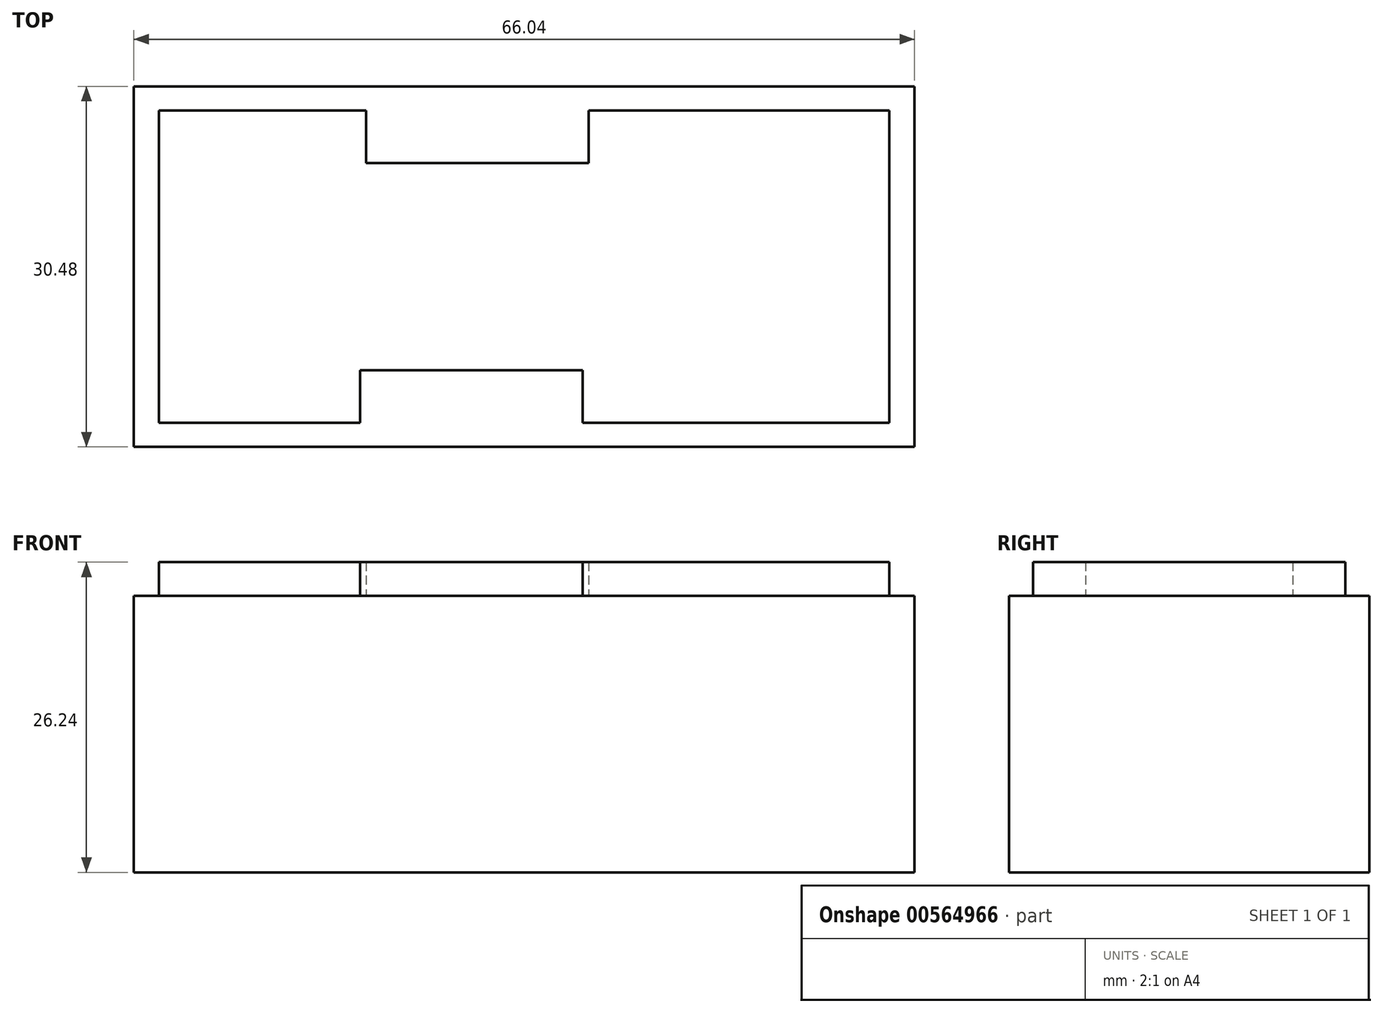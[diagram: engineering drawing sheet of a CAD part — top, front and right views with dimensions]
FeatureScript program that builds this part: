
annotation { "Feature Type Name" : "Feature", "Feature Type Description" : "" }
export const myFeature = defineFeature(function(context is Context, id is Id, definition is map)
    precondition{}
    {
        {
            var Q0;
            Q0=qCreatedBy(makeId("Top.planeOp"),FACE);
            var sketch = newSketch(context, id + "F0", { "sketchPlane" : qUnion([Q0])});
            skLineSegment(sketch, "E0.bottom", {"start": v(-27.3, 14.18) * mm, "end": v(38.75, 14.18) * mm});
            skLineSegment(sketch, "E0.top", {"start": v(-27.3, -16.3) * mm, "end": v(38.75, -16.3) * mm});
            skLineSegment(sketch, "E0.left", {"start": v(-27.3, 14.18) * mm, "end": v(-27.3, -16.3) * mm});
            skLineSegment(sketch, "E0.right", {"start": v(38.75, 14.18) * mm, "end": v(38.75, -16.3) * mm});
            skLineSegment(sketch, "E1.bottom", {"start": v(-25.16, 12.15) * mm, "end": v(36.62, 12.15) * mm});
            skLineSegment(sketch, "E1.top", {"start": v(-25.16, -14.27) * mm, "end": v(36.62, -14.27) * mm});
            skLineSegment(sketch, "E1.left", {"start": v(-25.16, 12.15) * mm, "end": v(-25.16, -14.27) * mm});
            skLineSegment(sketch, "E1.right", {"start": v(36.62, 12.15) * mm, "end": v(36.62, -14.27) * mm});
            skSolve(sketch);
        }
        {
            var Q0;
            Q0=makeQuery(id+"F0.imprint","IMPRINT",FACE,{"disambiguationData":[TD([[makeQuery(id+"F0.imprint","IMPRINT",EDGE,{"derivedFrom":sQuery(id+"F0.wireOp",EDGE,"E0.bottom")}),-1.0]])]});
            extrude(context, id + "F1", {"entities" : qUnion([Q0]), "depth" : 23.4 * mm, "offsetDistance" : 25.4 * mm});
        }
        {
            var Q0;
            Q0=makeQuery(id+"F0.imprint","IMPRINT",FACE,{"disambiguationData":[TD([[makeQuery(id+"F0.imprint","IMPRINT",EDGE,{"derivedFrom":sQuery(id+"F0.wireOp",EDGE,"E1.bottom")}),-1.0]])]});
            extrude(context, id + "F2", {"entities" : qUnion([Q0]), "operationType" : NewBodyOperationType.ADD, "depth" : 26.24 * mm, "offsetDistance" : 25.4 * mm});
        }
        {
            var Q0;
            Q0=makeQuery(id+"F2.opExtrude","SWEPT_FACE",FACE,{"disambiguationData":[OSD([sQuery(id+"F0.wireOp",EDGE,"E1.top")])]});
            var sketch = newSketch(context, id + "F3", { "sketchPlane" : qUnion([Q0])});
            skLineSegment(sketch, "E2.bottom", {"start": v(-8.16, 26.24) * mm, "end": v(10.68, 26.24) * mm});
            skLineSegment(sketch, "E2.top", {"start": v(-8.16, 23.4) * mm, "end": v(10.68, 23.4) * mm});
            skLineSegment(sketch, "E2.left", {"start": v(-8.16, 26.24) * mm, "end": v(-8.16, 23.4) * mm});
            skLineSegment(sketch, "E2.right", {"start": v(10.68, 26.24) * mm, "end": v(10.68, 23.4) * mm});
            skSolve(sketch);
        }
        {
            var Q0;
            Q0=makeQuery(id+"F3.imprint","IMPRINT",FACE,{"disambiguationData":[TD([[makeQuery(id+"F3.imprint","IMPRINT",EDGE,{"derivedFrom":sQuery(id+"F3.wireOp",EDGE,"E2.bottom")}),-1.0]])]});
            extrude(context, id + "F4", {"entities" : qUnion([Q0]), "operationType" : NewBodyOperationType.REMOVE, "oppositeDirection" : true, "depth" : 4.44 * mm, "offsetDistance" : 25.4 * mm});
        }
        {
            var Q0;
            Q0=makeQuery(id+"F2.opExtrude","SWEPT_FACE",FACE,{"disambiguationData":[OSD([sQuery(id+"F0.wireOp",EDGE,"E1.bottom")])]});
            var sketch = newSketch(context, id + "F5", { "sketchPlane" : qUnion([Q0])});
            skLineSegment(sketch, "E3.bottom", {"start": v(-11.2, 26.24) * mm, "end": v(7.66, 26.24) * mm});
            skLineSegment(sketch, "E3.top", {"start": v(-11.2, 23.4) * mm, "end": v(7.66, 23.4) * mm});
            skLineSegment(sketch, "E3.left", {"start": v(-11.2, 26.24) * mm, "end": v(-11.2, 23.4) * mm});
            skLineSegment(sketch, "E3.right", {"start": v(7.66, 26.24) * mm, "end": v(7.66, 23.4) * mm});
            skSolve(sketch);
        }
        {
            var Q0;
            Q0=makeQuery(id+"F5.imprint","IMPRINT",FACE,{"disambiguationData":[TD([[makeQuery(id+"F5.imprint","IMPRINT",EDGE,{"derivedFrom":sQuery(id+"F5.wireOp",EDGE,"E3.bottom")}),1.0]])]});
            extrude(context, id + "F6", {"entities" : qUnion([Q0]), "operationType" : NewBodyOperationType.REMOVE, "oppositeDirection" : true, "depth" : 4.44 * mm, "offsetDistance" : 25.4 * mm});
        }
    });
